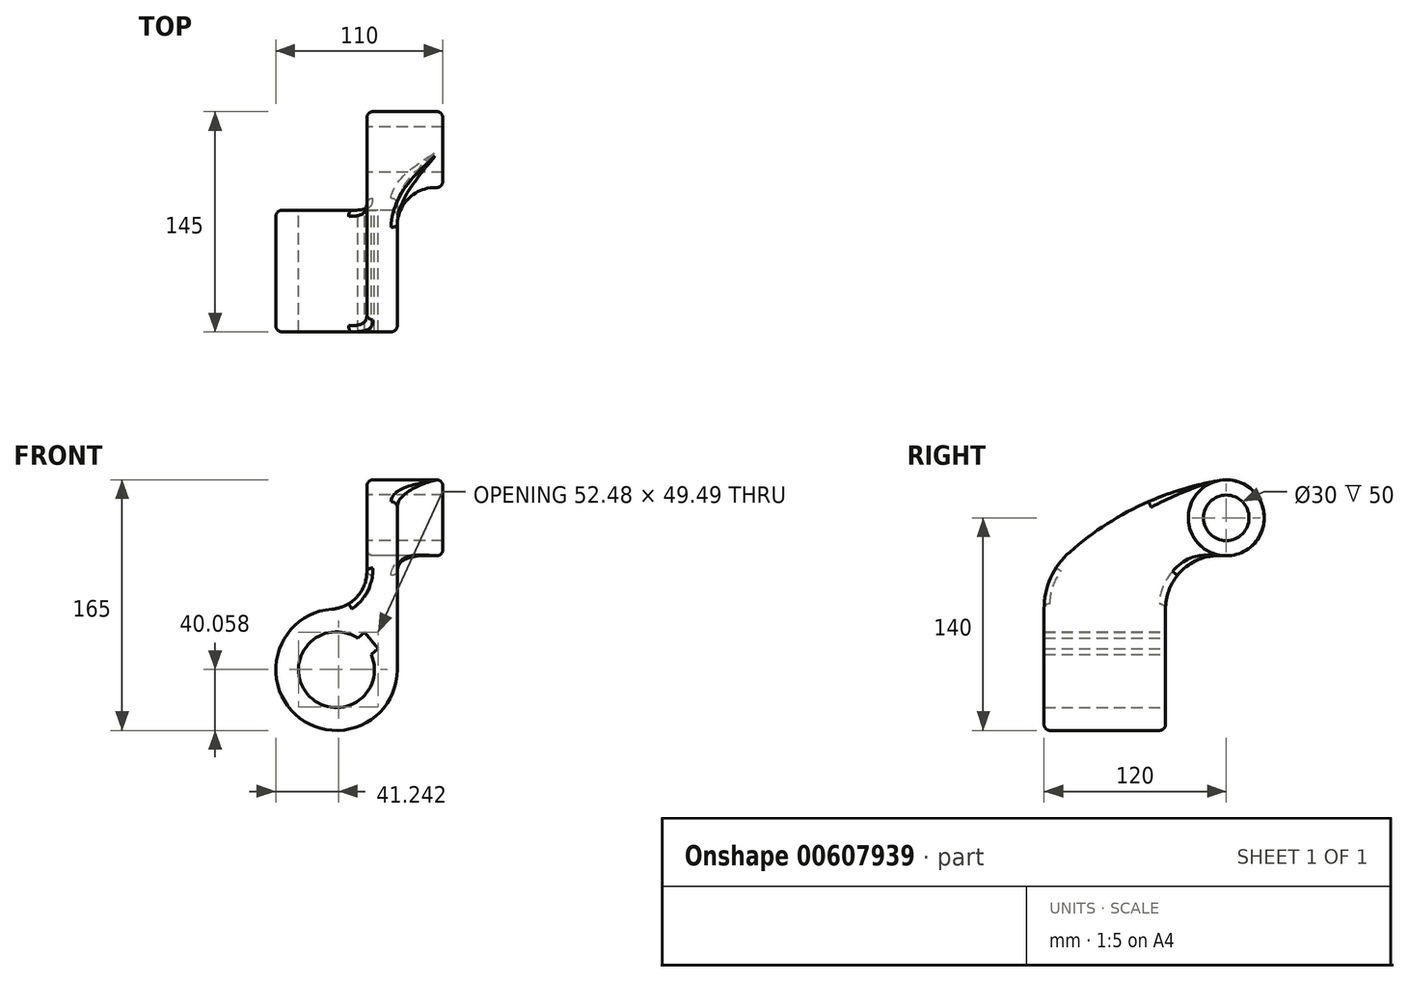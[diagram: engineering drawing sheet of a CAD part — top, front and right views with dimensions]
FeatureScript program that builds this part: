
annotation { "Feature Type Name" : "Feature", "Feature Type Description" : "" }
export const myFeature = defineFeature(function(context is Context, id is Id, definition is map)
    precondition{}
    {
        {
            var Q0;
            Q0=qCreatedBy(makeId("Right.planeOp"),FACE);
            var sketch = newSketch(context, id + "F0", { "sketchPlane" : qUnion([Q0])});
            skLineSegment(sketch, "E0", {"start": v(0, 0) * mm, "end": v(-80, 0) * mm});
            skLineSegment(sketch, "E1", {"start": v(-80, 0) * mm, "end": v(-80, 40) * mm});
            skLineSegment(sketch, "E2", {"start": v(-80, 40) * mm, "end": v(0, 40) * mm});
            skLineSegment(sketch, "E3", {"start": v(0, 40) * mm, "end": v(0, 0) * mm});
            skCircle(sketch, "E4", {"center": v(40, 100) * mm, "radius": 15 * mm});
            skCircle(sketch, "E5", {"center": v(40, 100) * mm, "radius": 25 * mm});
            skArc(sketch, "E6", {"start": v(38, 75.08) * mm, "mid": v(11.32, 65.86) * mm, "end": v(0, 40) * mm});
            skArc(sketch, "E7", {"start": v(-63.05, 77.52) * mm, "mid": v(-75.57, 60.58) * mm, "end": v(-80, 40) * mm});
            skArc(sketch, "E8", {"start": v(35.84, 124.65) * mm, "mid": v(-16.9, 107.99) * mm, "end": v(-63.05, 77.52) * mm});
            skSolve(sketch);
        }
        {
            var Q0;
            Q0=makeQuery(id+"F0.imprint","IMPRINT",FACE,{"disambiguationData":[TD([[makeQuery(id+"F0.imprint","IMPRINT",EDGE,{"derivedFrom":sQuery(id+"F0.wireOp",EDGE,"E4")}),-1.0]])]});
            extrude(context, id + "F1", {"entities" : qUnion([Q0]), "depth" : 50 * mm, "offsetDistance" : 25 * mm});
        }
        {
            var Q0;
            Q0 = qSketchRegion(id + "F0", true);
            extrude(context, id + "F2", {"entities" : qUnion([Q0]), "operationType" : NewBodyOperationType.ADD, "depth" : 20 * mm, "offsetDistance" : 25 * mm});
        }
        {
            var Q0;
            Q0=qCreatedBy(makeId("Front.planeOp"),FACE);
            var sketch = newSketch(context, id + "F3", { "sketchPlane" : qUnion([Q0])});
            skLineSegment(sketch, "E9", {"start": v(0, 0) * mm, "end": v(-20, 0) * mm, "construction": true});
            skCircle(sketch, "E10", {"center": v(-20, 0) * mm, "radius": 40 * mm});
            skCircle(sketch, "E11", {"center": v(-20, 0) * mm, "radius": 25 * mm});
            skLineSegment(sketch, "E12", {"start": v(-20, 0) * mm, "end": v(25.96, 38.57) * mm, "construction": true});
            skLineSegment(sketch, "E13", {"start": v(-0.85, 16.07) * mm, "end": v(2.98, 19.28) * mm});
            skLineSegment(sketch, "E14", {"start": v(2.98, 19.28) * mm, "end": v(7.48, 13.92) * mm});
            skLineSegment(sketch, "E15", {"start": v(7.48, 13.92) * mm, "end": v(2.88, 10.06) * mm});
            skLineSegment(sketch, "E16", {"start": v(2.98, 19.28) * mm, "end": v(-1.52, 24.65) * mm});
            skLineSegment(sketch, "E17", {"start": v(-1.52, 24.65) * mm, "end": v(-6.11, 20.79) * mm});
            skSolve(sketch);
        }
        {
            var Q0;
            Q0=makeQuery(id+"F3.imprint","IMPRINT",FACE,{"disambiguationData":[TD([[makeQuery(id+"F3.imprint","IMPRINT",EDGE,{"derivedFrom":sQuery(id+"F3.wireOp",EDGE,"E10")}),1.0]])]});
            extrude(context, id + "F4", {"entities" : qUnion([Q0]), "operationType" : NewBodyOperationType.ADD, "depth" : 80 * mm, "offsetDistance" : 25 * mm});
        }
        {
            var Q0;
            Q0=makeQuery(id+"F3.imprint","IMPRINT",FACE,{"disambiguationData":[TD([[makeQuery(id+"F3.imprint","IMPRINT",EDGE,{"derivedFrom":sQuery(id+"F3.wireOp",EDGE,"E11")}),1.0]])]});
            extrude(context, id + "F5", {"entities" : qUnion([Q0]), "operationType" : NewBodyOperationType.REMOVE, "depth" : 80 * mm, "offsetDistance" : 25 * mm});
        }
        {
            var Q0;
            {var subQ0=sQuery(id+"F0.wireOp",EDGE,"E5");Q0=makeQuery(id+"F2.boolean.opBoolean","INTERSECT",EDGE,{"derivedFrom":[makeQuery(id+"F1.opExtrude","SWEPT_FACE",FACE,{"disambiguationData":[OSD([subQ0])]}),makeQuery(id+"F2.opExtrude","CAP_FACE",FACE,{"disambiguationData":[OSD([sQuery(id+"F0.wireOp",EDGE,"E0"),sQuery(id+"F0.wireOp",EDGE,"E1"),sQuery(id+"F0.wireOp",EDGE,"E3"),sQuery(id+"F0.wireOp",EDGE,"E4"),subQ0,sQuery(id+"F0.wireOp",EDGE,"E6"),sQuery(id+"F0.wireOp",EDGE,"E7"),sQuery(id+"F0.wireOp",EDGE,"E8")])],"isStart":false})]});}
            fillet(context, id + "F6", {"entities" : qUnion([Q0]), "radius" : 25 * mm, "tangentPropagation" : true, "allowEdgeOverflow" : false});
        }
        {
            var Q0;
            {var subQ0=sQuery(id+"F3.wireOp",EDGE,"E13");Q0=makeQuery(id+"F3.imprint","IMPRINT",FACE,{"disambiguationData":[TD([[makeQuery(id+"F3.imprint","IMPRINT",EDGE,{"derivedFrom":subQ0}),-1.0]])]});}
            var Q1;
            {var subQ0=sQuery(id+"F3.wireOp",EDGE,"E13");Q1=makeQuery(id+"F3.imprint","IMPRINT",FACE,{"disambiguationData":[TD([[makeQuery(id+"F3.imprint","IMPRINT",EDGE,{"derivedFrom":subQ0}),1.0]])]});}
            extrude(context, id + "F7", {"entities" : qUnion([Q0, Q1]), "operationType" : NewBodyOperationType.REMOVE, "depth" : 80 * mm, "offsetDistance" : 25 * mm});
        }
        {
            var Q0;
            {var subQ0=sQuery(id+"F0.wireOp",EDGE,"E5");var subQ1=sQuery(id+"F0.wireOp",EDGE,"E4");Q0=makeQuery(id+"F4.boolean.opBoolean","INTERSECT",EDGE,{"derivedFrom":[makeQuery(id+"F2.boolean.opBoolean","MERGE",FACE,{"derivedFrom":[makeQuery(id+"F1.opExtrude","CAP_FACE",FACE,{"disambiguationData":[OSD([subQ1,subQ0])],"isStart":true}),makeQuery(id+"F2.opExtrude","CAP_FACE",FACE,{"disambiguationData":[OSD([sQuery(id+"F0.wireOp",EDGE,"E0"),sQuery(id+"F0.wireOp",EDGE,"E1"),sQuery(id+"F0.wireOp",EDGE,"E3"),subQ1,subQ0,sQuery(id+"F0.wireOp",EDGE,"E6"),sQuery(id+"F0.wireOp",EDGE,"E7"),sQuery(id+"F0.wireOp",EDGE,"E8")])],"isStart":true})]}),makeQuery(id+"F4.opExtrude","SWEPT_FACE",FACE,{"disambiguationData":[OSD([sQuery(id+"F3.wireOp",EDGE,"E10")])]})]});}
            fillet(context, id + "F8", {"entities" : qUnion([Q0]), "radius" : 25 * mm, "tangentPropagation" : true, "allowEdgeOverflow" : false});
        }
        {
            var Q0;
            Q0=makeQuery(id+"F4.opExtrude","CAP_EDGE",EDGE,{"disambiguationData":[OSD([sQuery(id+"F3.wireOp",EDGE,"E10")])],"isStart":false});
            var Q1;
            Q1=makeQuery(id+"F1.opExtrude","CAP_EDGE",EDGE,{"disambiguationData":[OSD([sQuery(id+"F0.wireOp",EDGE,"E5")])],"isStart":false});
            fillet(context, id + "F9", {"entities" : qUnion([Q0, Q1]), "radius" : 4 * mm, "tangentPropagation" : true, "allowEdgeOverflow" : false});
        }
    });
